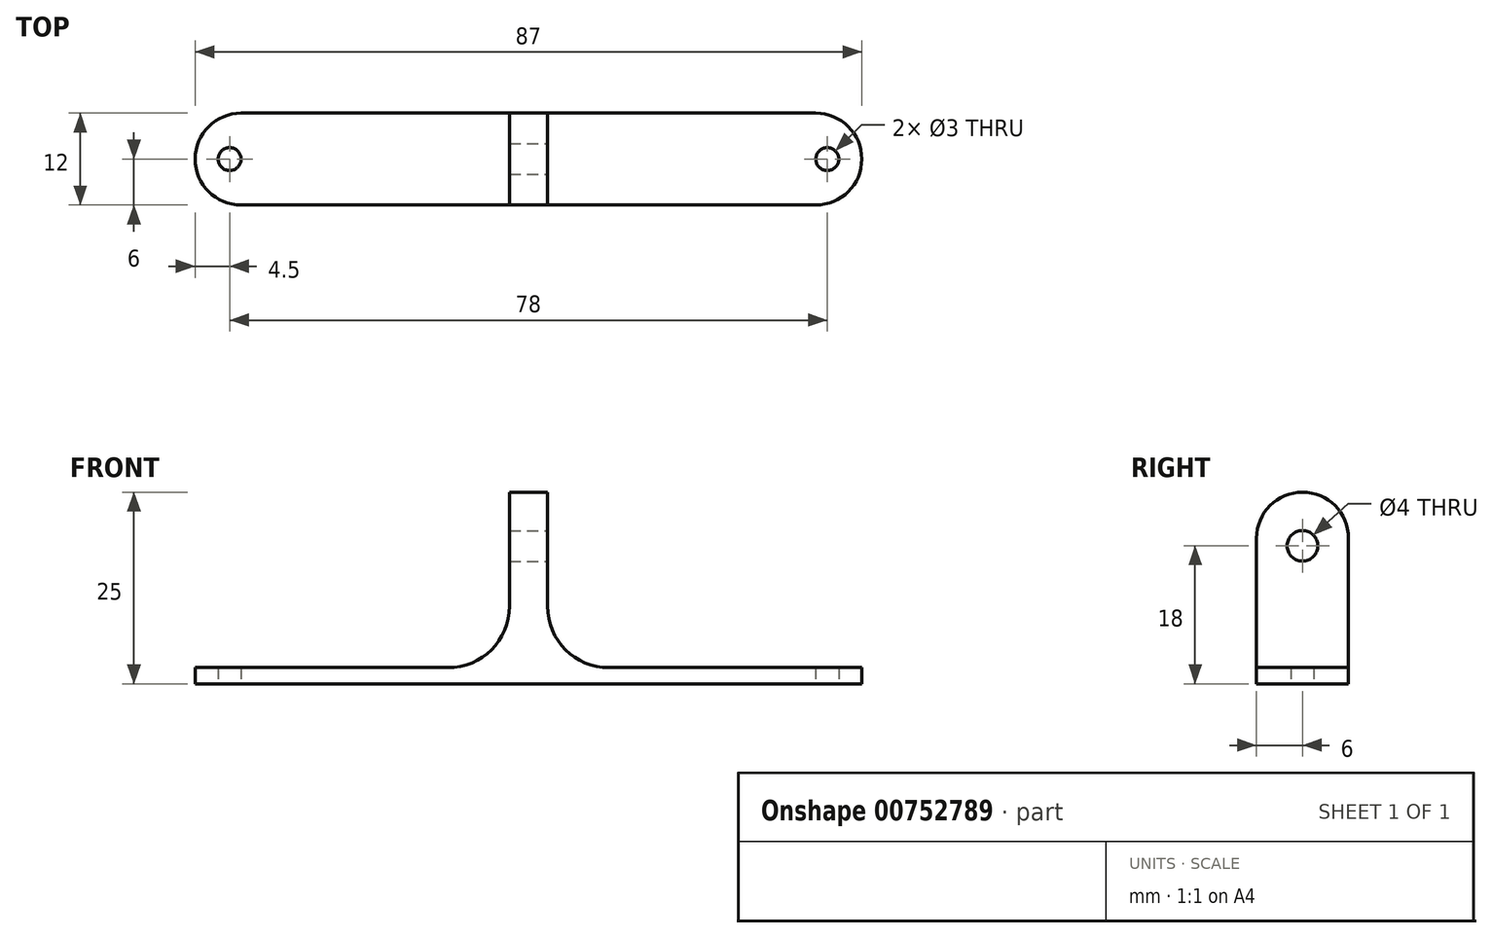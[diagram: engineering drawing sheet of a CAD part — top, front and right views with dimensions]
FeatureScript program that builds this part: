
annotation { "Feature Type Name" : "Feature", "Feature Type Description" : "" }
export const myFeature = defineFeature(function(context is Context, id is Id, definition is map)
    precondition{}
    {
        {
            var Q0;
            Q0=qCreatedBy(makeId("Top.planeOp"),FACE);
            var sketch = newSketch(context, id + "F0", { "sketchPlane" : qUnion([Q0])});
            skLineSegment(sketch, "E0.bottom", {"start": v(-43.5, -6) * mm, "end": v(43.5, -6) * mm});
            skLineSegment(sketch, "E0.top", {"start": v(-43.5, 6) * mm, "end": v(43.5, 6) * mm});
            skLineSegment(sketch, "E0.left", {"start": v(-43.5, -6) * mm, "end": v(-43.5, 6) * mm});
            skLineSegment(sketch, "E0.right", {"start": v(43.5, -6) * mm, "end": v(43.5, 6) * mm});
            skPoint(sketch, "E0.middle", {"position": v(0, 0) * mm});
            skLineSegment(sketch, "E1", {"start": v(0, 0) * mm, "end": v(-39, 0) * mm, "construction": true});
            skCircle(sketch, "E2", {"center": v(-39, 0) * mm, "radius": 1.5 * mm});
            skLineSegment(sketch, "E3", {"start": v(0, 0) * mm, "end": v(0, -2.7) * mm, "construction": true});
            skCircle(sketch, "E4.MirrorC", {"center": v(39, 0) * mm, "radius": 1.5 * mm});
            skLineSegment(sketch, "E5.bottom", {"start": v(-2.5, -6) * mm, "end": v(2.5, -6) * mm});
            skLineSegment(sketch, "E5.top", {"start": v(-2.5, 6) * mm, "end": v(2.5, 6) * mm});
            skLineSegment(sketch, "E5.left", {"start": v(-2.5, -6) * mm, "end": v(-2.5, 6) * mm});
            skLineSegment(sketch, "E5.right", {"start": v(2.5, -6) * mm, "end": v(2.5, 6) * mm});
            skSolve(sketch);
        }
        {
            var Q0;
            {var subQ0=sQuery(id+"F0.wireOp",EDGE,"E0.right");var subQ7=sQuery(id+"F0.wireOp",EDGE,"E5.left");var subQ10=makeQuery(id+"F0.imprint","IMPRINT",EDGE,{"derivedFrom":subQ7});var subQ11=sQuery(id+"F0.wireOp",EDGE,"E0.left");Q0=qUnion([makeQuery(id+"F0.imprint","IMPRINT",FACE,{"disambiguationData":[TD([[makeQuery(id+"F0.imprint","IMPRINT",EDGE,{"derivedFrom":subQ11}),-1.0]])]}),makeQuery(id+"F0.imprint","IMPRINT",FACE,{"disambiguationData":[TD([[subQ10,-1.0]])]}),makeQuery(id+"F0.imprint","IMPRINT",FACE,{"disambiguationData":[TD([[makeQuery(id+"F0.imprint","IMPRINT",EDGE,{"derivedFrom":subQ0}),1.0]])]})]);}
            extrude(context, id + "F1", {"entities" : qUnion([Q0]), "depth" : 2.1 * mm, "offsetDistance" : 25 * mm});
        }
        {
            var Q0;
            {var subQ2=sQuery(id+"F0.wireOp",EDGE,"E5.left");Q0=makeQuery(id+"F0.imprint","IMPRINT",FACE,{"disambiguationData":[TD([[makeQuery(id+"F0.imprint","IMPRINT",EDGE,{"derivedFrom":subQ2}),-1.0]])]});}
            extrude(context, id + "F2", {"entities" : qUnion([Q0]), "operationType" : NewBodyOperationType.ADD, "depth" : 25 * mm, "offsetDistance" : 25 * mm});
        }
        {
            var Q0;
            Q0=qCreatedBy(makeId("Right.planeOp"),FACE);
            var sketch = newSketch(context, id + "F3", { "sketchPlane" : qUnion([Q0])});
            skLineSegment(sketch, "E6", {"start": v(0, 0) * mm, "end": v(0, 18) * mm, "construction": true});
            skCircle(sketch, "E7", {"center": v(0, 18) * mm, "radius": 2 * mm});
            skSolve(sketch);
        }
        {
            var Q0;
            Q0=qSketchRegion(id+"F3",true);
            extrude(context, id + "F4", {"entities" : qUnion([Q0]), "operationType" : NewBodyOperationType.REMOVE, "endBound" : BoundingType.SYMMETRIC, "oppositeDirection" : true, "depth" : 25 * mm, "offsetDistance" : 25 * mm});
        }
        {
            var Q0;
            Q0=makeQuery(id+"F2.opExtrude","CAP_EDGE",EDGE,{"disambiguationData":[OSD([sQuery(id+"F0.wireOp",EDGE,"E0.bottom")])],"isStart":false});
            var Q1;
            Q1=makeQuery(id+"F2.opExtrude","CAP_EDGE",EDGE,{"disambiguationData":[OSD([sQuery(id+"F0.wireOp",EDGE,"E0.top")])],"isStart":false});
            var Q2;
            Q2=makeQuery(id+"F1.opExtrude","SWEPT_EDGE",EDGE,{"disambiguationData":[OSD([sQuery(id+"F0.wireOp",EDGE,"E0.bottom"),sQuery(id+"F0.wireOp",EDGE,"E0.left")])]});
            var Q3;
            Q3=makeQuery(id+"F1.opExtrude","SWEPT_EDGE",EDGE,{"disambiguationData":[OSD([sQuery(id+"F0.wireOp",EDGE,"E0.top"),sQuery(id+"F0.wireOp",EDGE,"E0.left")])]});
            var Q4;
            Q4=makeQuery(id+"F1.opExtrude","SWEPT_EDGE",EDGE,{"disambiguationData":[OSD([sQuery(id+"F0.wireOp",EDGE,"E0.bottom"),sQuery(id+"F0.wireOp",EDGE,"E0.right")])]});
            var Q5;
            Q5=makeQuery(id+"F1.opExtrude","SWEPT_EDGE",EDGE,{"disambiguationData":[OSD([sQuery(id+"F0.wireOp",EDGE,"E0.top"),sQuery(id+"F0.wireOp",EDGE,"E0.right")])]});
            fillet(context, id + "F5", {"entities" : qUnion([Q0, Q1, Q2, Q3, Q4, Q5]), "radius" : 6 * mm, "tangentPropagation" : true, "allowEdgeOverflow" : false});
        }
        {
            var Q0;
            Q0=makeQuery(id+"F2.boolean.opBoolean","INTERSECT",EDGE,{"derivedFrom":[makeQuery(id+"F1.opExtrude","CAP_FACE",FACE,{"disambiguationData":[OSD([sQuery(id+"F0.wireOp",EDGE,"E0.bottom"),sQuery(id+"F0.wireOp",EDGE,"E0.top"),sQuery(id+"F0.wireOp",EDGE,"E0.left"),sQuery(id+"F0.wireOp",EDGE,"E0.right"),sQuery(id+"F0.wireOp",EDGE,"E2"),sQuery(id+"F0.wireOp",EDGE,"E4.MirrorC")])],"isStart":false}),makeQuery(id+"F2.opExtrude","SWEPT_FACE",FACE,{"disambiguationData":[OSD([sQuery(id+"F0.wireOp",EDGE,"E5.right")])]})]});
            var Q1;
            Q1=makeQuery(id+"F2.boolean.opBoolean","INTERSECT",EDGE,{"derivedFrom":[makeQuery(id+"F1.opExtrude","CAP_FACE",FACE,{"disambiguationData":[OSD([sQuery(id+"F0.wireOp",EDGE,"E0.bottom"),sQuery(id+"F0.wireOp",EDGE,"E0.top"),sQuery(id+"F0.wireOp",EDGE,"E0.left"),sQuery(id+"F0.wireOp",EDGE,"E0.right"),sQuery(id+"F0.wireOp",EDGE,"E2"),sQuery(id+"F0.wireOp",EDGE,"E4.MirrorC")])],"isStart":false}),makeQuery(id+"F2.opExtrude","SWEPT_FACE",FACE,{"disambiguationData":[OSD([sQuery(id+"F0.wireOp",EDGE,"E5.left")])]})]});
            fillet(context, id + "F6", {"entities" : qUnion([Q0, Q1]), "radius" : 8 * mm, "tangentPropagation" : true, "allowEdgeOverflow" : false});
        }
    });
